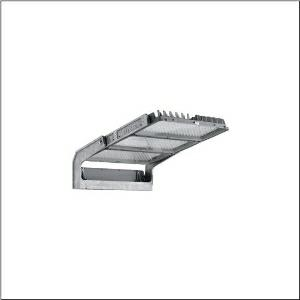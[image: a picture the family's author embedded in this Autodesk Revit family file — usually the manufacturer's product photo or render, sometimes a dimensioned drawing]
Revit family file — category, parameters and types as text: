
# Revit family: floodlight_fl_11_maxi_pro___rs08_5xa779124l02fb_fdbd
name_source: partatom
category: Lighting Fixtures
units: mm (PartAtom-declared; Revit-internal decimal feet)

## family parameters
Cut with Voids When Loaded = No
Host = Face
Light Source = No
Part Type = Normal
Room Calculation Point = No
Round Connector Dimension = Use Diameter
Shared = No

## types (1)
- --- (1 x LED, 129490 lm, 1323.9 W, 5700K)
    Apparent Load = 1324 VA
    CIE Flux Codes = 70 87 98 100 100
    Color Rendering = 90
    Color Temperature = 5700K
    Default Elevation = 1800 mm
    Description = Floodlight FL 11  maxi  pro floodlight; light control with lens of PMMA; cover panel of toughened safety glass, transparent; light distribution: RS08, rotationally symmetric direct distribution, LEDcolour temperature: 5700K, rated luminous flux: 129.490lm, colour rendering: CRI > 90, light colour: 957; luminous efficacy: 98lm/W; brightness control: DALI 2; with terminal, 5-pole, max. 2.5mm², mains connection: 220..240V/380..400V AC, 50/60Hz, surge voltage resistance: line to ground: 10kV, service life up to 100,000h L90. Typical operating time: 1000h per year, ECG replaceable separately, LED unit replaceable without ESD environment, dustproof LED module, dimming range 10..100%; 1324W floodlight with 3x LED unit of diecast aluminium, coated grey; length: 1.003mm / width: 651mm / height: 338mm; mounting bracket, of diecast aluminium, uncoated, natural, protection rating (complete): IP66; insulation class (complete): insulation class I (protective earthing); certification: CE, ENEC, VDE; ball protection: ball impact resistant, only for outdoor installations in the designated locations, permissible operating ambient temperature: -45..+55°C, permissible storage temperature: -40..+85°Cpackaging unit: 1 piece

Light Distribution: RS08
    Height = 320 mm
    Lamp = 1 x LED
    Lamp Light Flux = 129490 lm
    Lamp Power = 1323.9 W
    Lamp count = 1
    Length = 1002 mm
    Luminous efficacy = 98 lm/W
    Manufacturer = Siteco
    ModVariant = No
    Model = 5XA779124L02FB
    Mounting Place = Ceiling
    Mounting Type = Surface mounted
    Number of Poles = 1
    OnlyDefault = Yes
    Power Factor = 1
    Product Name = Floodlight FL 11 maxi pro | RS08
    Product group = floodlight | ceiling mounted
    ProductGroupID = 301
    Protection Class = Protection class I
    Protection Degree = IP 66
    RLX_Detail_Level = 1
    RLX_Emergency_Light_Flux = 0 lm
    RLX_Emergency_Type = 0
    RLX_Emergency_Type_DB = No
    RlxData = <blob elided: 40405 chars, md5=4986bdd4>
    Socket = socket
    Standby Power = 0 W
    System Light Flux = 129490 lm
    System Power = 1324 W
    Type Comments = factory setting: luminous flux: 100 % | dim-lin: 254 | 900 mA
    Type Image = l_1356210.jpg
    URL = http://relux.com
    VarID = @adj_024760
    Voltage = 0 V
    Weight = 0.00 kg
    Width = 655 mm

## geometry (parser evidence)
native form markers: Blend x4, Sweep x12
no freeform markers — native parametric forms only
